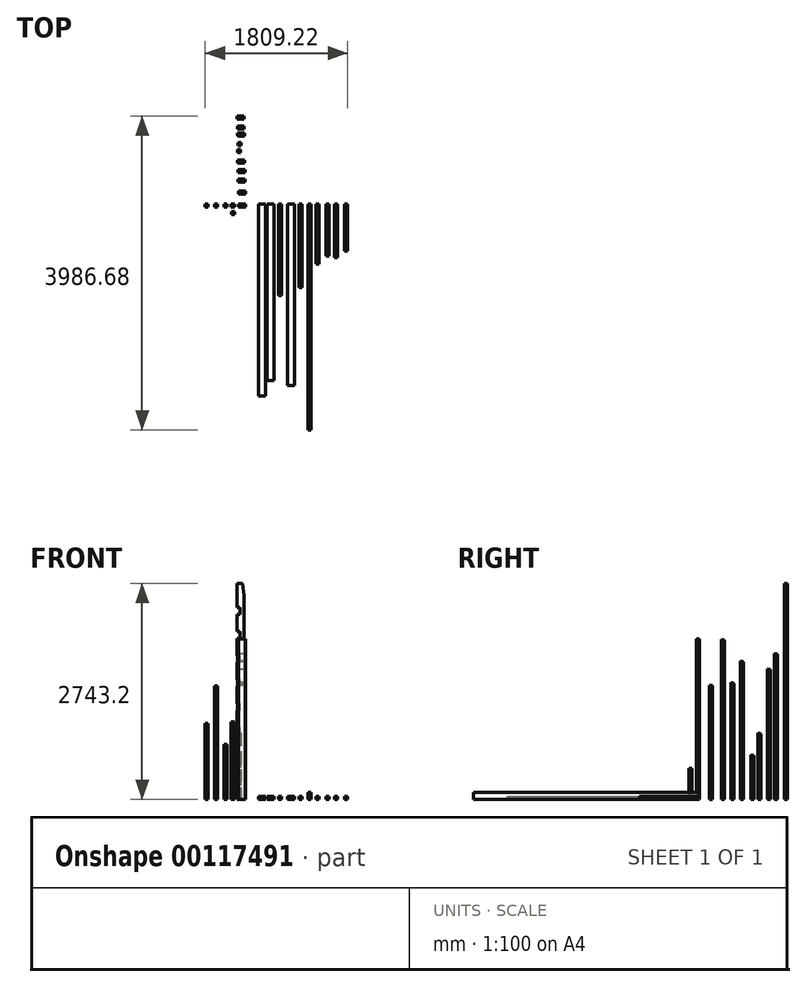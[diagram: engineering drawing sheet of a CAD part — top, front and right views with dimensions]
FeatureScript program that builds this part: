
annotation { "Feature Type Name" : "Feature", "Feature Type Description" : "" }
export const myFeature = defineFeature(function(context is Context, id is Id, definition is map)
    precondition{}
    {
        {
            var Q0;
            Q0=qCreatedBy(makeId("Front.planeOp"),FACE);
            var sketch = newSketch(context, id + "F0", { "sketchPlane" : qUnion([Q0])});
            skLineSegment(sketch, "E0.bottom", {"start": v(0, 0) * mm, "end": v(88.9, 0) * mm});
            skLineSegment(sketch, "E0.top", {"start": v(0, 38.1) * mm, "end": v(88.9, 38.1) * mm});
            skLineSegment(sketch, "E0.left", {"start": v(0, 0) * mm, "end": v(0, 38.1) * mm});
            skLineSegment(sketch, "E0.right", {"start": v(88.9, 0) * mm, "end": v(88.9, 38.1) * mm});
            skSolve(sketch);
        }
        {
            var Q0;
            Q0=makeQuery(id+"F0.imprint","IMPRINT",FACE,{"disambiguationData":[TD([[makeQuery(id+"F0.imprint","IMPRINT",EDGE,{"derivedFrom":sQuery(id+"F0.wireOp",EDGE,"E0.bottom")}),1.0]])]});
            extrude(context, id + "F1", {"entities" : qUnion([Q0]), "depth" : 2438.4 * mm});
        }
        {
            var Q0;
            Q0=qCreatedBy(makeId("Front.planeOp"),FACE);
            var sketch = newSketch(context, id + "F2", { "sketchPlane" : qUnion([Q0])});
            skLineSegment(sketch, "E1.bottom", {"start": v(106.96, 0) * mm, "end": v(195.86, 0) * mm});
            skLineSegment(sketch, "E1.top", {"start": v(106.96, 38.1) * mm, "end": v(195.86, 38.1) * mm});
            skLineSegment(sketch, "E1.left", {"start": v(106.96, 0) * mm, "end": v(106.96, 38.1) * mm});
            skLineSegment(sketch, "E1.right", {"start": v(195.86, 0) * mm, "end": v(195.86, 38.1) * mm});
            skSolve(sketch);
        }
        {
            var Q0;
            Q0=makeQuery(id+"F2.imprint","IMPRINT",FACE,{"disambiguationData":[TD([[makeQuery(id+"F2.imprint","IMPRINT",EDGE,{"derivedFrom":sQuery(id+"F2.wireOp",EDGE,"E1.bottom")}),1.0]])]});
            extrude(context, id + "F3", {"entities" : qUnion([Q0]), "depth" : 2241.55 * mm});
        }
        {
            var Q0;
            Q0=qCreatedBy(makeId("Top.planeOp"),FACE);
            var sketch = newSketch(context, id + "F4", { "sketchPlane" : qUnion([Q0])});
            skLineSegment(sketch, "E2.bottom", {"start": v(-166.18, 0) * mm, "end": v(-255.08, 0) * mm});
            skLineSegment(sketch, "E2.top", {"start": v(-166.18, -38.1) * mm, "end": v(-255.08, -38.1) * mm});
            skLineSegment(sketch, "E2.left", {"start": v(-166.18, 0) * mm, "end": v(-166.18, -38.1) * mm});
            skLineSegment(sketch, "E2.right", {"start": v(-255.08, 0) * mm, "end": v(-255.08, -38.1) * mm});
            skSolve(sketch);
        }
        {
            var Q0;
            Q0=makeQuery(id+"F4.imprint","IMPRINT",FACE,{"disambiguationData":[TD([[makeQuery(id+"F4.imprint","IMPRINT",EDGE,{"derivedFrom":sQuery(id+"F4.wireOp",EDGE,"E2.bottom")}),1.0]])]});
            extrude(context, id + "F5", {"entities" : qUnion([Q0]), "depth" : 2038.35 * mm});
        }
        {
            var Q0;
            Q0=qCreatedBy(makeId("Front.planeOp"),FACE);
            var sketch = newSketch(context, id + "F6", { "sketchPlane" : qUnion([Q0])});
            skLineSegment(sketch, "E3.bottom", {"start": v(255.76, 0) * mm, "end": v(293.86, 0) * mm});
            skLineSegment(sketch, "E3.top", {"start": v(255.76, 38.1) * mm, "end": v(293.86, 38.1) * mm});
            skLineSegment(sketch, "E3.left", {"start": v(255.76, 0) * mm, "end": v(255.76, 38.1) * mm});
            skLineSegment(sketch, "E3.right", {"start": v(293.86, 0) * mm, "end": v(293.86, 38.1) * mm});
            skSolve(sketch);
        }
        {
            var Q0;
            Q0=makeQuery(id+"F6.imprint","IMPRINT",FACE,{"disambiguationData":[TD([[makeQuery(id+"F6.imprint","IMPRINT",EDGE,{"derivedFrom":sQuery(id+"F6.wireOp",EDGE,"E3.bottom")}),1.0]])]});
            extrude(context, id + "F7", {"entities" : qUnion([Q0]), "depth" : 1162.05 * mm});
        }
        {
            var Q0;
            Q0=qCreatedBy(makeId("Top.planeOp"),FACE);
            var sketch = newSketch(context, id + "F8", { "sketchPlane" : qUnion([Q0])});
            skLineSegment(sketch, "E4.bottom", {"start": v(-308.68, 0) * mm, "end": v(-346.78, 0) * mm});
            skLineSegment(sketch, "E4.top", {"start": v(-308.68, -38.1) * mm, "end": v(-346.78, -38.1) * mm});
            skLineSegment(sketch, "E4.left", {"start": v(-308.68, 0) * mm, "end": v(-308.68, -38.1) * mm});
            skLineSegment(sketch, "E4.right", {"start": v(-346.78, 0) * mm, "end": v(-346.78, -38.1) * mm});
            skSolve(sketch);
        }
        {
            var Q0;
            Q0=makeQuery(id+"F8.imprint","IMPRINT",FACE,{"disambiguationData":[TD([[makeQuery(id+"F8.imprint","IMPRINT",EDGE,{"derivedFrom":sQuery(id+"F8.wireOp",EDGE,"E4.bottom")}),1.0]])]});
            extrude(context, id + "F9", {"entities" : qUnion([Q0]), "depth" : 984.25 * mm});
        }
        {
            var Q0;
            Q0=qCreatedBy(makeId("Top.planeOp"),FACE);
            var sketch = newSketch(context, id + "F10", { "sketchPlane" : qUnion([Q0])});
            skLineSegment(sketch, "E5.bottom", {"start": v(-399.06, 0) * mm, "end": v(-437.16, 0) * mm});
            skLineSegment(sketch, "E5.top", {"start": v(-399.06, -38.1) * mm, "end": v(-437.16, -38.1) * mm});
            skLineSegment(sketch, "E5.left", {"start": v(-399.06, 0) * mm, "end": v(-399.06, -38.1) * mm});
            skLineSegment(sketch, "E5.right", {"start": v(-437.16, 0) * mm, "end": v(-437.16, -38.1) * mm});
            skSolve(sketch);
        }
        {
            var Q0;
            Q0=makeQuery(id+"F10.imprint","IMPRINT",FACE,{"disambiguationData":[TD([[makeQuery(id+"F10.imprint","IMPRINT",EDGE,{"derivedFrom":sQuery(id+"F10.wireOp",EDGE,"E5.bottom")}),1.0]])]});
            extrude(context, id + "F11", {"entities" : qUnion([Q0]), "depth" : 698.5 * mm});
        }
        {
            var Q0;
            Q0=qCreatedBy(makeId("Top.planeOp"),FACE);
            var sketch = newSketch(context, id + "F12", { "sketchPlane" : qUnion([Q0])});
            skLineSegment(sketch, "E6.bottom", {"start": v(-164.7, 125.57) * mm, "end": v(-253.6, 125.57) * mm});
            skLineSegment(sketch, "E6.top", {"start": v(-164.7, 163.67) * mm, "end": v(-253.6, 163.67) * mm});
            skLineSegment(sketch, "E6.left", {"start": v(-164.7, 125.57) * mm, "end": v(-164.7, 163.67) * mm});
            skLineSegment(sketch, "E6.right", {"start": v(-253.6, 125.57) * mm, "end": v(-253.6, 163.67) * mm});
            skSolve(sketch);
        }
        {
            var Q0;
            Q0=makeQuery(id+"F12.imprint","IMPRINT",FACE,{"disambiguationData":[TD([[makeQuery(id+"F12.imprint","IMPRINT",EDGE,{"derivedFrom":sQuery(id+"F12.wireOp",EDGE,"E6.bottom")}),-1.0]])]});
            extrude(context, id + "F13", {"entities" : qUnion([Q0]), "depth" : 1447.8 * mm});
        }
        {
            var Q0;
            Q0=qCreatedBy(makeId("Top.planeOp"),FACE);
            var sketch = newSketch(context, id + "F14", { "sketchPlane" : qUnion([Q0])});
            skLineSegment(sketch, "E7.bottom", {"start": v(-343.83, -96.28) * mm, "end": v(-305.73, -96.28) * mm});
            skLineSegment(sketch, "E7.top", {"start": v(-343.83, -134.38) * mm, "end": v(-305.73, -134.38) * mm});
            skLineSegment(sketch, "E7.left", {"start": v(-343.83, -96.28) * mm, "end": v(-343.83, -134.38) * mm});
            skLineSegment(sketch, "E7.right", {"start": v(-305.73, -96.28) * mm, "end": v(-305.73, -134.38) * mm});
            skSolve(sketch);
        }
        {
            var Q0;
            Q0=makeQuery(id+"F14.imprint","IMPRINT",FACE,{"disambiguationData":[TD([[makeQuery(id+"F14.imprint","IMPRINT",EDGE,{"derivedFrom":sQuery(id+"F14.wireOp",EDGE,"E7.bottom")}),-1.0]])]});
            extrude(context, id + "F15", {"entities" : qUnion([Q0]), "depth" : 393.7 * mm});
        }
        {
            var Q0;
            Q0=qCreatedBy(makeId("Top.planeOp"),FACE);
            var sketch = newSketch(context, id + "F16", { "sketchPlane" : qUnion([Q0])});
            skLineSegment(sketch, "E8.bottom", {"start": v(-172.33, 276.56) * mm, "end": v(-261.23, 276.56) * mm});
            skLineSegment(sketch, "E8.top", {"start": v(-172.33, 314.66) * mm, "end": v(-261.23, 314.66) * mm});
            skLineSegment(sketch, "E8.left", {"start": v(-172.33, 276.56) * mm, "end": v(-172.33, 314.66) * mm});
            skLineSegment(sketch, "E8.right", {"start": v(-261.23, 276.56) * mm, "end": v(-261.23, 314.66) * mm});
            skSolve(sketch);
        }
        {
            var Q0;
            Q0=makeQuery(id+"F16.imprint","IMPRINT",FACE,{"disambiguationData":[TD([[makeQuery(id+"F16.imprint","IMPRINT",EDGE,{"derivedFrom":sQuery(id+"F16.wireOp",EDGE,"E8.bottom")}),-1.0]])]});
            extrude(context, id + "F17", {"entities" : qUnion([Q0]), "depth" : 2032 * mm});
        }
        {
            var Q0;
            Q0=makeQuery(id+"F17.opExtrude","SWEPT_FACE",FACE,{"disambiguationData":[OSD([sQuery(id+"F16.wireOp",EDGE,"E8.right")])]});
            var sketch = newSketch(context, id + "F18", { "sketchPlane" : qUnion([Q0])});
            skLineSegment(sketch, "E9", {"start": v(-276.56, 2032) * mm, "end": v(-314.66, 2022.47) * mm});
            skLineSegment(sketch, "E10", {"start": v(-314.66, 2022.47) * mm, "end": v(-314.66, 2032) * mm});
            skLineSegment(sketch, "E11", {"start": v(-314.66, 2032) * mm, "end": v(-276.56, 2032) * mm});
            skSolve(sketch);
        }
        {
            var Q0;
            Q0=makeQuery(id+"F18.imprint","IMPRINT",FACE,{"disambiguationData":[TD([[makeQuery(id+"F18.imprint","IMPRINT",EDGE,{"derivedFrom":sQuery(id+"F18.wireOp",EDGE,"E9")}),-1.0]])]});
            extrude(context, id + "F19", {"entities" : qUnion([Q0]), "operationType" : NewBodyOperationType.REMOVE, "oppositeDirection" : true, "depth" : 101.6 * mm});
        }
        {
            var Q0;
            Q0=qCreatedBy(makeId("Top.planeOp"),FACE);
            var sketch = newSketch(context, id + "F20", { "sketchPlane" : qUnion([Q0])});
            skLineSegment(sketch, "E12.bottom", {"start": v(-170.25, 397.07) * mm, "end": v(-259.15, 397.07) * mm});
            skLineSegment(sketch, "E12.top", {"start": v(-170.25, 435.17) * mm, "end": v(-259.15, 435.17) * mm});
            skLineSegment(sketch, "E12.left", {"start": v(-170.25, 397.07) * mm, "end": v(-170.25, 435.17) * mm});
            skLineSegment(sketch, "E12.right", {"start": v(-259.15, 397.07) * mm, "end": v(-259.15, 435.17) * mm});
            skSolve(sketch);
        }
        {
            var Q0;
            Q0=makeQuery(id+"F20.imprint","IMPRINT",FACE,{"disambiguationData":[TD([[makeQuery(id+"F20.imprint","IMPRINT",EDGE,{"derivedFrom":sQuery(id+"F20.wireOp",EDGE,"E12.bottom")}),-1.0]])]});
            extrude(context, id + "F21", {"entities" : qUnion([Q0]), "depth" : 1482.72 * mm});
        }
        {
            var Q0;
            Q0=makeQuery(id+"F21.opExtrude","SWEPT_FACE",FACE,{"disambiguationData":[OSD([sQuery(id+"F20.wireOp",EDGE,"E12.right")])]});
            var sketch = newSketch(context, id + "F22", { "sketchPlane" : qUnion([Q0])});
            skLineSegment(sketch, "E13", {"start": v(-397.07, 1482.73) * mm, "end": v(-435.17, 1473.2) * mm});
            skLineSegment(sketch, "E14", {"start": v(-435.17, 1473.2) * mm, "end": v(-435.17, 1482.73) * mm});
            skLineSegment(sketch, "E15", {"start": v(-435.17, 1482.73) * mm, "end": v(-397.07, 1482.73) * mm});
            skSolve(sketch);
        }
        {
            var Q0;
            Q0=makeQuery(id+"F22.imprint","IMPRINT",FACE,{"disambiguationData":[TD([[makeQuery(id+"F22.imprint","IMPRINT",EDGE,{"derivedFrom":sQuery(id+"F22.wireOp",EDGE,"E13")}),-1.0]])]});
            extrude(context, id + "F23", {"entities" : qUnion([Q0]), "operationType" : NewBodyOperationType.REMOVE, "oppositeDirection" : true, "depth" : 101.6 * mm});
        }
        {
            var Q0;
            Q0=qCreatedBy(makeId("Front.planeOp"),FACE);
            var sketch = newSketch(context, id + "F24", { "sketchPlane" : qUnion([Q0])});
            skLineSegment(sketch, "E16.bottom", {"start": v(367.17, 0) * mm, "end": v(456.07, 0) * mm});
            skLineSegment(sketch, "E16.top", {"start": v(367.17, 38.1) * mm, "end": v(456.07, 38.1) * mm});
            skLineSegment(sketch, "E16.left", {"start": v(367.17, 0) * mm, "end": v(367.17, 38.1) * mm});
            skLineSegment(sketch, "E16.right", {"start": v(456.07, 0) * mm, "end": v(456.07, 38.1) * mm});
            skSolve(sketch);
        }
        {
            var Q0;
            Q0=makeQuery(id+"F24.imprint","IMPRINT",FACE,{"disambiguationData":[TD([[makeQuery(id+"F24.imprint","IMPRINT",EDGE,{"derivedFrom":sQuery(id+"F24.wireOp",EDGE,"E16.bottom")}),1.0]])]});
            extrude(context, id + "F25", {"entities" : qUnion([Q0]), "depth" : 2305.05 * mm});
        }
        {
            var Q0;
            Q0=qCreatedBy(makeId("Top.planeOp"),FACE);
            var sketch = newSketch(context, id + "F26", { "sketchPlane" : qUnion([Q0])});
            skLineSegment(sketch, "E17.bottom", {"start": v(-175.87, 520.72) * mm, "end": v(-264.77, 520.72) * mm});
            skLineSegment(sketch, "E17.top", {"start": v(-175.87, 558.82) * mm, "end": v(-264.77, 558.82) * mm});
            skLineSegment(sketch, "E17.left", {"start": v(-175.87, 520.72) * mm, "end": v(-175.87, 558.82) * mm});
            skLineSegment(sketch, "E17.right", {"start": v(-264.77, 520.72) * mm, "end": v(-264.77, 558.82) * mm});
            skSolve(sketch);
        }
        {
            var Q0;
            Q0=makeQuery(id+"F26.imprint","IMPRINT",FACE,{"disambiguationData":[TD([[makeQuery(id+"F26.imprint","IMPRINT",EDGE,{"derivedFrom":sQuery(id+"F26.wireOp",EDGE,"E17.bottom")}),-1.0]])]});
            extrude(context, id + "F27", {"entities" : qUnion([Q0]), "depth" : 1757.36 * mm});
        }
        {
            var Q0;
            Q0=makeQuery(id+"F27.opExtrude","SWEPT_FACE",FACE,{"disambiguationData":[OSD([sQuery(id+"F26.wireOp",EDGE,"E17.right")])]});
            var sketch = newSketch(context, id + "F28", { "sketchPlane" : qUnion([Q0])});
            skLineSegment(sketch, "E18", {"start": v(-520.72, 1757.36) * mm, "end": v(-558.82, 1747.84) * mm});
            skLineSegment(sketch, "E19", {"start": v(-558.82, 1747.84) * mm, "end": v(-558.82, 1757.36) * mm});
            skLineSegment(sketch, "E20", {"start": v(-558.82, 1757.36) * mm, "end": v(-520.72, 1757.36) * mm});
            skSolve(sketch);
        }
        {
            var Q0;
            Q0=makeQuery(id+"F28.imprint","IMPRINT",FACE,{"disambiguationData":[TD([[makeQuery(id+"F28.imprint","IMPRINT",EDGE,{"derivedFrom":sQuery(id+"F28.wireOp",EDGE,"E18")}),-1.0]])]});
            extrude(context, id + "F29", {"entities" : qUnion([Q0]), "operationType" : NewBodyOperationType.REMOVE, "oppositeDirection" : true, "depth" : 88.9 * mm});
        }
        {
            var Q0;
            Q0=qCreatedBy(makeId("Front.planeOp"),FACE);
            var sketch = newSketch(context, id + "F30", { "sketchPlane" : qUnion([Q0])});
            skLineSegment(sketch, "E21.bottom", {"start": v(516.07, 0) * mm, "end": v(554.17, 0) * mm});
            skLineSegment(sketch, "E21.top", {"start": v(516.07, 38.1) * mm, "end": v(554.17, 38.1) * mm});
            skLineSegment(sketch, "E21.left", {"start": v(516.07, 0) * mm, "end": v(516.07, 38.1) * mm});
            skLineSegment(sketch, "E21.right", {"start": v(554.17, 0) * mm, "end": v(554.17, 38.1) * mm});
            skSolve(sketch);
        }
        {
            var Q0;
            Q0=makeQuery(id+"F30.imprint","IMPRINT",FACE,{"disambiguationData":[TD([[makeQuery(id+"F30.imprint","IMPRINT",EDGE,{"derivedFrom":sQuery(id+"F30.wireOp",EDGE,"E21.bottom")}),1.0]])]});
            extrude(context, id + "F31", {"entities" : qUnion([Q0]), "depth" : 1063.62 * mm});
        }
        {
            var Q0;
            Q0=qCreatedBy(makeId("Top.planeOp"),FACE);
            var sketch = newSketch(context, id + "F32", { "sketchPlane" : qUnion([Q0])});
            skLineSegment(sketch, "E22.bottom", {"start": v(-226.42, 650.27) * mm, "end": v(-264.52, 650.27) * mm});
            skLineSegment(sketch, "E22.top", {"start": v(-226.42, 688.37) * mm, "end": v(-264.52, 688.37) * mm});
            skLineSegment(sketch, "E22.left", {"start": v(-226.42, 650.27) * mm, "end": v(-226.42, 688.37) * mm});
            skLineSegment(sketch, "E22.right", {"start": v(-264.52, 650.27) * mm, "end": v(-264.52, 688.37) * mm});
            skSolve(sketch);
        }
        {
            var Q0;
            Q0=makeQuery(id+"F32.imprint","IMPRINT",FACE,{"disambiguationData":[TD([[makeQuery(id+"F32.imprint","IMPRINT",EDGE,{"derivedFrom":sQuery(id+"F32.wireOp",EDGE,"E22.bottom")}),-1.0]])]});
            extrude(context, id + "F33", {"entities" : qUnion([Q0]), "depth" : 565.15 * mm});
        }
        {
            var Q0;
            Q0=makeQuery(id+"F33.opExtrude","SWEPT_FACE",FACE,{"disambiguationData":[OSD([sQuery(id+"F32.wireOp",EDGE,"E22.right")])]});
            var sketch = newSketch(context, id + "F34", { "sketchPlane" : qUnion([Q0])});
            skLineSegment(sketch, "E23", {"start": v(-650.27, 565.15) * mm, "end": v(-688.37, 555.63) * mm});
            skLineSegment(sketch, "E24", {"start": v(-688.37, 555.62) * mm, "end": v(-688.37, 565.15) * mm});
            skLineSegment(sketch, "E25", {"start": v(-688.37, 565.15) * mm, "end": v(-650.27, 565.15) * mm});
            skSolve(sketch);
        }
        {
            var Q0;
            Q0=makeQuery(id+"F34.imprint","IMPRINT",FACE,{"disambiguationData":[TD([[makeQuery(id+"F34.imprint","IMPRINT",EDGE,{"derivedFrom":sQuery(id+"F34.wireOp",EDGE,"E23")}),-1.0]])]});
            extrude(context, id + "F35", {"entities" : qUnion([Q0]), "operationType" : NewBodyOperationType.REMOVE, "oppositeDirection" : true, "depth" : 101.6 * mm});
        }
        {
            var Q0;
            Q0=qCreatedBy(makeId("Top.planeOp"),FACE);
            var sketch = newSketch(context, id + "F36", { "sketchPlane" : qUnion([Q0])});
            skLineSegment(sketch, "E26.bottom", {"start": v(-262.78, 742.65) * mm, "end": v(-224.68, 742.65) * mm});
            skLineSegment(sketch, "E26.top", {"start": v(-262.78, 780.75) * mm, "end": v(-224.68, 780.75) * mm});
            skLineSegment(sketch, "E26.left", {"start": v(-262.78, 742.65) * mm, "end": v(-262.78, 780.75) * mm});
            skLineSegment(sketch, "E26.right", {"start": v(-224.68, 742.65) * mm, "end": v(-224.68, 780.75) * mm});
            skSolve(sketch);
        }
        {
            var Q0;
            Q0=makeQuery(id+"F36.imprint","IMPRINT",FACE,{"disambiguationData":[TD([[makeQuery(id+"F36.imprint","IMPRINT",EDGE,{"derivedFrom":sQuery(id+"F36.wireOp",EDGE,"E26.bottom")}),1.0]])]});
            extrude(context, id + "F37", {"entities" : qUnion([Q0]), "depth" : 841.38 * mm});
        }
        {
            var Q0;
            Q0=makeQuery(id+"F37.opExtrude","SWEPT_FACE",FACE,{"disambiguationData":[OSD([sQuery(id+"F36.wireOp",EDGE,"E26.left")])]});
            var sketch = newSketch(context, id + "F38", { "sketchPlane" : qUnion([Q0])});
            skLineSegment(sketch, "E27", {"start": v(-742.65, 841.38) * mm, "end": v(-780.75, 831.85) * mm});
            skLineSegment(sketch, "E28", {"start": v(-780.75, 831.85) * mm, "end": v(-780.75, 841.38) * mm});
            skLineSegment(sketch, "E29", {"start": v(-780.75, 841.38) * mm, "end": v(-742.65, 841.38) * mm});
            skSolve(sketch);
        }
        {
            var Q0;
            Q0=makeQuery(id+"F38.imprint","IMPRINT",FACE,{"disambiguationData":[TD([[makeQuery(id+"F38.imprint","IMPRINT",EDGE,{"derivedFrom":sQuery(id+"F38.wireOp",EDGE,"E27")}),-1.0]])]});
            extrude(context, id + "F39", {"entities" : qUnion([Q0]), "operationType" : NewBodyOperationType.REMOVE, "oppositeDirection" : true, "depth" : 38.1 * mm});
        }
        {
            var Q0;
            Q0=qCreatedBy(makeId("Front.planeOp"),FACE);
            var sketch = newSketch(context, id + "F40", { "sketchPlane" : qUnion([Q0])});
            skLineSegment(sketch, "E30.bottom", {"start": v(630.28, 0) * mm, "end": v(668.38, 0) * mm});
            skLineSegment(sketch, "E30.top", {"start": v(630.28, 88.9) * mm, "end": v(668.38, 88.9) * mm});
            skLineSegment(sketch, "E30.left", {"start": v(630.28, 0) * mm, "end": v(630.28, 88.9) * mm});
            skLineSegment(sketch, "E30.right", {"start": v(668.38, 0) * mm, "end": v(668.38, 88.9) * mm});
            skSolve(sketch);
        }
        {
            var Q0;
            Q0=makeQuery(id+"F40.imprint","IMPRINT",FACE,{"disambiguationData":[TD([[makeQuery(id+"F40.imprint","IMPRINT",EDGE,{"derivedFrom":sQuery(id+"F40.wireOp",EDGE,"E30.bottom")}),1.0]])]});
            extrude(context, id + "F41", {"entities" : qUnion([Q0]), "depth" : 2870.2 * mm});
        }
        {
            var Q0;
            Q0=qCreatedBy(makeId("Top.planeOp"),FACE);
            var sketch = newSketch(context, id + "F42", { "sketchPlane" : qUnion([Q0])});
            skLineSegment(sketch, "E31.bottom", {"start": v(-269.18, 864.95) * mm, "end": v(-180.28, 864.95) * mm});
            skLineSegment(sketch, "E31.top", {"start": v(-269.18, 903.05) * mm, "end": v(-180.28, 903.05) * mm});
            skLineSegment(sketch, "E31.left", {"start": v(-269.18, 864.95) * mm, "end": v(-269.18, 903.05) * mm});
            skLineSegment(sketch, "E31.right", {"start": v(-180.28, 864.95) * mm, "end": v(-180.28, 903.05) * mm});
            skSolve(sketch);
        }
        {
            var Q0;
            Q0=makeQuery(id+"F42.imprint","IMPRINT",FACE,{"disambiguationData":[TD([[makeQuery(id+"F42.imprint","IMPRINT",EDGE,{"derivedFrom":sQuery(id+"F42.wireOp",EDGE,"E31.bottom")}),1.0]])]});
            extrude(context, id + "F43", {"entities" : qUnion([Q0]), "depth" : 1658.62 * mm});
        }
        {
            var Q0;
            Q0=makeQuery(id+"F43.opExtrude","SWEPT_FACE",FACE,{"disambiguationData":[OSD([sQuery(id+"F42.wireOp",EDGE,"E31.left")])]});
            var sketch = newSketch(context, id + "F44", { "sketchPlane" : qUnion([Q0])});
            skLineSegment(sketch, "E32", {"start": v(-864.95, 1658.62) * mm, "end": v(-903.05, 1649.1) * mm});
            skLineSegment(sketch, "E33", {"start": v(-903.05, 1649.1) * mm, "end": v(-903.05, 1658.62) * mm});
            skLineSegment(sketch, "E34", {"start": v(-903.05, 1658.62) * mm, "end": v(-864.95, 1658.62) * mm});
            skSolve(sketch);
        }
        {
            var Q0;
            Q0=makeQuery(id+"F44.imprint","IMPRINT",FACE,{"disambiguationData":[TD([[makeQuery(id+"F44.imprint","IMPRINT",EDGE,{"derivedFrom":sQuery(id+"F44.wireOp",EDGE,"E32")}),-1.0]])]});
            extrude(context, id + "F45", {"entities" : qUnion([Q0]), "operationType" : NewBodyOperationType.REMOVE, "oppositeDirection" : true, "depth" : 88.9 * mm});
        }
        {
            var Q0;
            Q0=qCreatedBy(makeId("Top.planeOp"),FACE);
            var sketch = newSketch(context, id + "F46", { "sketchPlane" : qUnion([Q0])});
            skLineSegment(sketch, "E35.bottom", {"start": v(-270.34, 989.5) * mm, "end": v(-181.44, 989.5) * mm});
            skLineSegment(sketch, "E35.top", {"start": v(-270.34, 951.4) * mm, "end": v(-181.44, 951.4) * mm});
            skLineSegment(sketch, "E35.left", {"start": v(-270.34, 989.5) * mm, "end": v(-270.34, 951.4) * mm});
            skLineSegment(sketch, "E35.right", {"start": v(-181.44, 989.5) * mm, "end": v(-181.44, 951.4) * mm});
            skSolve(sketch);
        }
        {
            var Q0;
            Q0=makeQuery(id+"F46.imprint","IMPRINT",FACE,{"disambiguationData":[TD([[makeQuery(id+"F46.imprint","IMPRINT",EDGE,{"derivedFrom":sQuery(id+"F46.wireOp",EDGE,"E35.bottom")}),-1.0]])]});
            extrude(context, id + "F47", {"entities" : qUnion([Q0]), "depth" : 1854.2 * mm});
        }
        {
            var Q0;
            Q0=makeQuery(id+"F47.opExtrude","SWEPT_FACE",FACE,{"disambiguationData":[OSD([sQuery(id+"F46.wireOp",EDGE,"E35.left")])]});
            var sketch = newSketch(context, id + "F48", { "sketchPlane" : qUnion([Q0])});
            skLineSegment(sketch, "E36", {"start": v(-951.4, 1854.2) * mm, "end": v(-989.5, 1844.67) * mm});
            skLineSegment(sketch, "E37", {"start": v(-989.5, 1844.67) * mm, "end": v(-989.5, 1854.2) * mm});
            skLineSegment(sketch, "E38", {"start": v(-989.5, 1854.2) * mm, "end": v(-951.4, 1854.2) * mm});
            skSolve(sketch);
        }
        {
            var Q0;
            Q0=makeQuery(id+"F48.imprint","IMPRINT",FACE,{"disambiguationData":[TD([[makeQuery(id+"F48.imprint","IMPRINT",EDGE,{"derivedFrom":sQuery(id+"F48.wireOp",EDGE,"E36")}),-1.0]])]});
            extrude(context, id + "F49", {"entities" : qUnion([Q0]), "operationType" : NewBodyOperationType.REMOVE, "oppositeDirection" : true, "depth" : 88.9 * mm});
        }
        {
            var Q0;
            Q0=qCreatedBy(makeId("Front.planeOp"),FACE);
            var sketch = newSketch(context, id + "F50", { "sketchPlane" : qUnion([Q0])});
            skLineSegment(sketch, "E39.bottom", {"start": v(730.15, 0) * mm, "end": v(768.25, 0) * mm});
            skLineSegment(sketch, "E39.top", {"start": v(730.15, 38.1) * mm, "end": v(768.25, 38.1) * mm});
            skLineSegment(sketch, "E39.left", {"start": v(730.15, 0) * mm, "end": v(730.15, 38.1) * mm});
            skLineSegment(sketch, "E39.right", {"start": v(768.25, 0) * mm, "end": v(768.25, 38.1) * mm});
            skSolve(sketch);
        }
        {
            var Q0;
            Q0=makeQuery(id+"F50.imprint","IMPRINT",FACE,{"disambiguationData":[TD([[makeQuery(id+"F50.imprint","IMPRINT",EDGE,{"derivedFrom":sQuery(id+"F50.wireOp",EDGE,"E39.bottom")}),1.0]])]});
            extrude(context, id + "F51", {"entities" : qUnion([Q0]), "depth" : 762 * mm});
        }
        {
            var Q0;
            Q0=qCreatedBy(makeId("Front.planeOp"),FACE);
            var sketch = newSketch(context, id + "F52", { "sketchPlane" : qUnion([Q0])});
            skLineSegment(sketch, "E40.bottom", {"start": v(855.17, 0) * mm, "end": v(893.27, 0) * mm});
            skLineSegment(sketch, "E40.top", {"start": v(855.17, 38.1) * mm, "end": v(893.27, 38.1) * mm});
            skLineSegment(sketch, "E40.left", {"start": v(855.17, 0) * mm, "end": v(855.17, 38.1) * mm});
            skLineSegment(sketch, "E40.right", {"start": v(893.27, 0) * mm, "end": v(893.27, 38.1) * mm});
            skSolve(sketch);
        }
        {
            var Q0;
            Q0=makeQuery(id+"F52.imprint","IMPRINT",FACE,{"disambiguationData":[TD([[makeQuery(id+"F52.imprint","IMPRINT",EDGE,{"derivedFrom":sQuery(id+"F52.wireOp",EDGE,"E40.bottom")}),1.0]])]});
            extrude(context, id + "F53", {"entities" : qUnion([Q0]), "depth" : 663.57 * mm});
        }
        {
            var Q0;
            Q0=qCreatedBy(makeId("Top.planeOp"),FACE);
            var sketch = newSketch(context, id + "F54", { "sketchPlane" : qUnion([Q0])});
            skLineSegment(sketch, "E41.bottom", {"start": v(-520.29, 0) * mm, "end": v(-558.39, 0) * mm});
            skLineSegment(sketch, "E41.top", {"start": v(-520.29, -38.1) * mm, "end": v(-558.39, -38.1) * mm});
            skLineSegment(sketch, "E41.left", {"start": v(-520.29, 0) * mm, "end": v(-520.29, -38.1) * mm});
            skLineSegment(sketch, "E41.right", {"start": v(-558.39, 0) * mm, "end": v(-558.39, -38.1) * mm});
            skSolve(sketch);
        }
        {
            var Q0;
            Q0=makeQuery(id+"F54.imprint","IMPRINT",FACE,{"disambiguationData":[TD([[makeQuery(id+"F54.imprint","IMPRINT",EDGE,{"derivedFrom":sQuery(id+"F54.wireOp",EDGE,"E41.bottom")}),1.0]])]});
            extrude(context, id + "F55", {"entities" : qUnion([Q0]), "depth" : 1441.45 * mm});
        }
        {
            var Q0;
            Q0=qCreatedBy(makeId("Front.planeOp"),FACE);
            var sketch = newSketch(context, id + "F56", { "sketchPlane" : qUnion([Q0])});
            skLineSegment(sketch, "E42.bottom", {"start": v(967.57, 0) * mm, "end": v(1005.67, 0) * mm});
            skLineSegment(sketch, "E42.top", {"start": v(967.57, 38.1) * mm, "end": v(1005.67, 38.1) * mm});
            skLineSegment(sketch, "E42.left", {"start": v(967.57, 0) * mm, "end": v(967.57, 38.1) * mm});
            skLineSegment(sketch, "E42.right", {"start": v(1005.67, 0) * mm, "end": v(1005.67, 38.1) * mm});
            skSolve(sketch);
        }
        {
            var Q0;
            Q0=makeQuery(id+"F56.imprint","IMPRINT",FACE,{"disambiguationData":[TD([[makeQuery(id+"F56.imprint","IMPRINT",EDGE,{"derivedFrom":sQuery(id+"F56.wireOp",EDGE,"E42.bottom")}),1.0]])]});
            extrude(context, id + "F57", {"entities" : qUnion([Q0]), "depth" : 679.45 * mm});
        }
        {
            var Q0;
            Q0=qCreatedBy(makeId("Front.planeOp"),FACE);
            var sketch = newSketch(context, id + "F58", { "sketchPlane" : qUnion([Q0])});
            skLineSegment(sketch, "E43.bottom", {"start": v(1093.12, 0) * mm, "end": v(1131.22, 0) * mm});
            skLineSegment(sketch, "E43.top", {"start": v(1093.12, 38.1) * mm, "end": v(1131.22, 38.1) * mm});
            skLineSegment(sketch, "E43.left", {"start": v(1093.12, 0) * mm, "end": v(1093.12, 38.1) * mm});
            skLineSegment(sketch, "E43.right", {"start": v(1131.22, 0) * mm, "end": v(1131.22, 38.1) * mm});
            skSolve(sketch);
        }
        {
            var Q0;
            Q0=makeQuery(id+"F58.imprint","IMPRINT",FACE,{"disambiguationData":[TD([[makeQuery(id+"F58.imprint","IMPRINT",EDGE,{"derivedFrom":sQuery(id+"F58.wireOp",EDGE,"E43.bottom")}),1.0]])]});
            extrude(context, id + "F59", {"entities" : qUnion([Q0]), "depth" : 600.07 * mm});
        }
        {
            var Q0;
            Q0=qCreatedBy(makeId("Top.planeOp"),FACE);
            var sketch = newSketch(context, id + "F60", { "sketchPlane" : qUnion([Q0])});
            skLineSegment(sketch, "E44.bottom", {"start": v(-639.9, 0) * mm, "end": v(-678, 0) * mm});
            skLineSegment(sketch, "E44.top", {"start": v(-639.9, -38.1) * mm, "end": v(-678, -38.1) * mm});
            skLineSegment(sketch, "E44.left", {"start": v(-639.9, 0) * mm, "end": v(-639.9, -38.1) * mm});
            skLineSegment(sketch, "E44.right", {"start": v(-678, 0) * mm, "end": v(-678, -38.1) * mm});
            skSolve(sketch);
        }
        {
            var Q0;
            Q0=makeQuery(id+"F60.imprint","IMPRINT",FACE,{"disambiguationData":[TD([[makeQuery(id+"F60.imprint","IMPRINT",EDGE,{"derivedFrom":sQuery(id+"F60.wireOp",EDGE,"E44.bottom")}),1.0]])]});
            extrude(context, id + "F61", {"entities" : qUnion([Q0]), "depth" : 965.2 * mm});
        }
        {
            var Q0;
            Q0=qCreatedBy(makeId("Top.planeOp"),FACE);
            var sketch = newSketch(context, id + "F62", { "sketchPlane" : qUnion([Q0])});
            skLineSegment(sketch, "E45.bottom", {"start": v(-186.15, 1078.38) * mm, "end": v(-275.05, 1078.38) * mm});
            skLineSegment(sketch, "E45.top", {"start": v(-186.15, 1116.48) * mm, "end": v(-275.05, 1116.48) * mm});
            skLineSegment(sketch, "E45.left", {"start": v(-186.15, 1078.38) * mm, "end": v(-186.15, 1116.48) * mm});
            skLineSegment(sketch, "E45.right", {"start": v(-275.05, 1078.38) * mm, "end": v(-275.05, 1116.48) * mm});
            skSolve(sketch);
        }
        {
            var Q0;
            Q0=makeQuery(id+"F62.imprint","IMPRINT",FACE,{"disambiguationData":[TD([[makeQuery(id+"F62.imprint","IMPRINT",EDGE,{"derivedFrom":sQuery(id+"F62.wireOp",EDGE,"E45.bottom")}),-1.0]])]});
            extrude(context, id + "F63", {"entities" : qUnion([Q0]), "depth" : 2743.2 * mm});
        }
        {
            var Q0;
            Q0=makeQuery(id+"F63.opExtrude","SWEPT_FACE",FACE,{"disambiguationData":[OSD([sQuery(id+"F62.wireOp",EDGE,"E45.top")])]});
            var sketch = newSketch(context, id + "F64", { "sketchPlane" : qUnion([Q0])});
            skLineSegment(sketch, "E46", {"start": v(186.15, 2590.8) * mm, "end": v(186.15, 2743.2) * mm});
            skLineSegment(sketch, "E47", {"start": v(186.15, 2743.2) * mm, "end": v(205.2, 2743.2) * mm});
            skLineSegment(sketch, "E48", {"start": v(205.2, 2743.2) * mm, "end": v(186.15, 2590.8) * mm});
            skLineSegment(sketch, "E49.bottom", {"start": v(275.05, 215.9) * mm, "end": v(236.95, 215.9) * mm});
            skLineSegment(sketch, "E49.top", {"start": v(275.05, 304.8) * mm, "end": v(236.95, 304.8) * mm});
            skLineSegment(sketch, "E49.left", {"start": v(275.05, 215.9) * mm, "end": v(275.05, 304.8) * mm});
            skLineSegment(sketch, "E49.right", {"start": v(236.95, 215.9) * mm, "end": v(236.95, 304.8) * mm});
            skLineSegment(sketch, "E50.bottom", {"start": v(275.05, 520.7) * mm, "end": v(236.95, 520.7) * mm});
            skLineSegment(sketch, "E50.top", {"start": v(275.05, 609.6) * mm, "end": v(236.95, 609.6) * mm});
            skLineSegment(sketch, "E50.left", {"start": v(275.05, 520.7) * mm, "end": v(275.05, 609.6) * mm});
            skLineSegment(sketch, "E50.right", {"start": v(236.95, 520.7) * mm, "end": v(236.95, 609.6) * mm});
            skLineSegment(sketch, "E51.bottom", {"start": v(275.05, 825.5) * mm, "end": v(236.95, 825.5) * mm});
            skLineSegment(sketch, "E51.top", {"start": v(275.05, 914.4) * mm, "end": v(236.95, 914.4) * mm});
            skLineSegment(sketch, "E51.left", {"start": v(275.05, 825.5) * mm, "end": v(275.05, 914.4) * mm});
            skLineSegment(sketch, "E51.right", {"start": v(236.95, 825.5) * mm, "end": v(236.95, 914.4) * mm});
            skPoint(sketch, "E52.oppositeSnap0", {"position": v(236.95, 869.95) * mm});
            skLineSegment(sketch, "E52.bottom", {"start": v(275.05, 1219.2) * mm, "end": v(236.95, 1219.2) * mm});
            skLineSegment(sketch, "E52.top", {"start": v(275.05, 1130.3) * mm, "end": v(236.95, 1130.3) * mm});
            skLineSegment(sketch, "E52.left", {"start": v(275.05, 1130.3) * mm, "end": v(275.05, 1219.2) * mm});
            skLineSegment(sketch, "E52.right", {"start": v(236.95, 1130.3) * mm, "end": v(236.95, 1219.2) * mm});
            skLineSegment(sketch, "E53.bottom", {"start": v(275.05, 1435.1) * mm, "end": v(236.95, 1435.1) * mm});
            skLineSegment(sketch, "E53.top", {"start": v(275.05, 1524) * mm, "end": v(236.95, 1524) * mm});
            skLineSegment(sketch, "E53.left", {"start": v(275.05, 1435.1) * mm, "end": v(275.05, 1524) * mm});
            skLineSegment(sketch, "E53.right", {"start": v(236.95, 1435.1) * mm, "end": v(236.95, 1524) * mm});
            skLineSegment(sketch, "E54.bottom", {"start": v(275.05, 1739.9) * mm, "end": v(236.95, 1739.9) * mm});
            skLineSegment(sketch, "E54.top", {"start": v(275.05, 1828.8) * mm, "end": v(236.95, 1828.8) * mm});
            skLineSegment(sketch, "E54.left", {"start": v(275.05, 1739.9) * mm, "end": v(275.05, 1828.8) * mm});
            skLineSegment(sketch, "E54.right", {"start": v(236.95, 1739.9) * mm, "end": v(236.95, 1828.8) * mm});
            skLineSegment(sketch, "E55.bottom", {"start": v(275.05, 2044.7) * mm, "end": v(236.95, 2044.7) * mm});
            skLineSegment(sketch, "E55.top", {"start": v(275.05, 2133.6) * mm, "end": v(236.95, 2133.6) * mm});
            skLineSegment(sketch, "E55.left", {"start": v(275.05, 2044.7) * mm, "end": v(275.05, 2133.6) * mm});
            skLineSegment(sketch, "E55.right", {"start": v(236.95, 2044.7) * mm, "end": v(236.95, 2133.6) * mm});
            skLineSegment(sketch, "E56.bottom", {"start": v(275.05, 2349.5) * mm, "end": v(236.95, 2349.5) * mm});
            skLineSegment(sketch, "E56.top", {"start": v(275.05, 2438.4) * mm, "end": v(236.95, 2438.4) * mm});
            skLineSegment(sketch, "E56.left", {"start": v(275.05, 2349.5) * mm, "end": v(275.05, 2438.4) * mm});
            skLineSegment(sketch, "E56.right", {"start": v(236.95, 2349.5) * mm, "end": v(236.95, 2438.4) * mm});
            skSolve(sketch);
        }
        {
            var Q0;
            Q0 = qSketchRegion(id + "F64", true);
            extrude(context, id + "F65", {"entities" : qUnion([Q0]), "operationType" : NewBodyOperationType.REMOVE, "oppositeDirection" : true, "depth" : 38.1 * mm});
        }
    });
